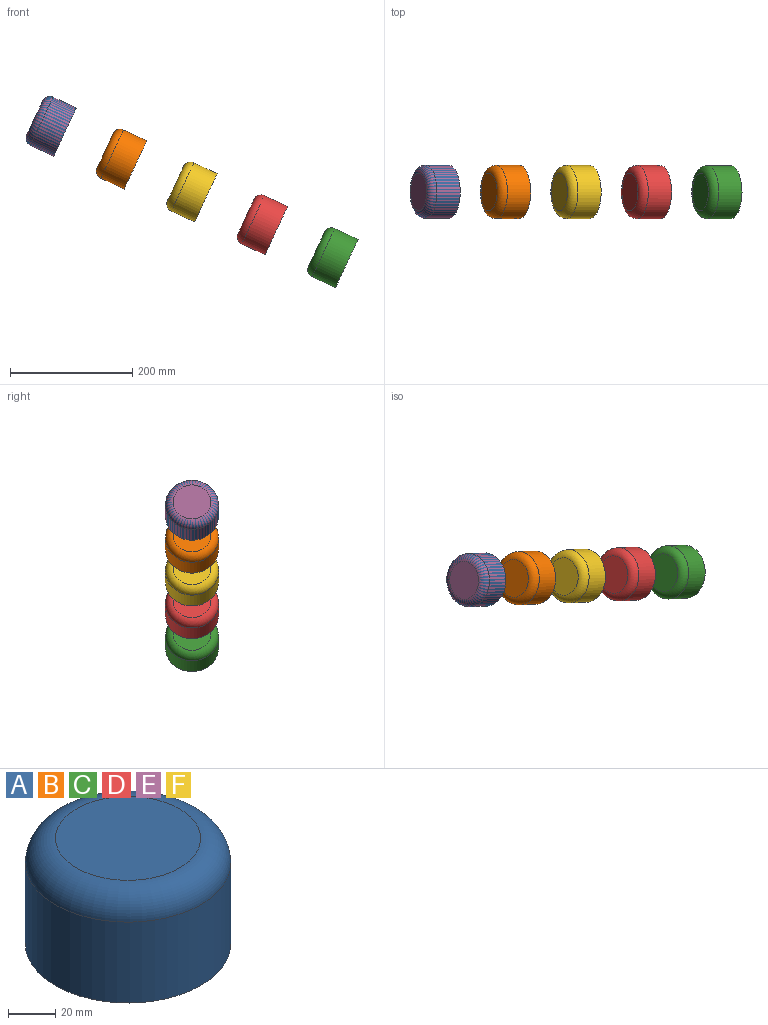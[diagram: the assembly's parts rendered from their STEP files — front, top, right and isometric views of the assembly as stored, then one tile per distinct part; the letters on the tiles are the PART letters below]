
ASSEMBLY  parts=6 mates=1
PART A: 4 faces, bbox 94x94x54.6 mm
  f0: cylinder r=43.44mm len=86.89mm, axis (0,0,-1), area 11440.1mm2, adj f2,f3
  f1: plane 61.49x61.49mm, normal (0,0,1), area 2969.4mm2, adj f3
  f2: plane 86.89x86.89mm, normal (0,0,-1), area 5929.4mm2, adj f0
  f3: torus R=30.74mm, axis (0,0,1), area 4867mm2, adj f0,f1
PART B: same geometry as A
PART C: same geometry as A
PART D: same geometry as A
PART E: same geometry as A
PART F: same geometry as A
PLACE A rot(axis=(0,-1,0),65deg) t=(18.78,-142.4,193.85)mm
PLACE B rot(axis=(0,-1,0),65deg) t=(133.88,-142.4,140.17)mm
PLACE C rot(axis=(0,-1,0),65deg) t=(479.18,-142.4,-20.84)mm
PLACE D rot(axis=(0,-1,0),65deg) t=(364.08,-142.4,32.83)mm
PLACE E rot(axis=(0,-1,0),65deg) t=(18.78,-142.4,193.85)mm
PLACE F rot(axis=(0,-1,0),65deg) t=(248.98,-142.4,86.5)mm
MATE revolute A.f0 <-> E.f0  axis (0.91,0,-0.42) through (-34.81,-142.4,78.93)mm
